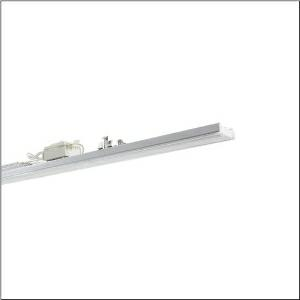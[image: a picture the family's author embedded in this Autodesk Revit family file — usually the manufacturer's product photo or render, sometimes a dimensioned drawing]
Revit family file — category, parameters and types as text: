
# Revit family: licross_r__21_recessed_mo_52te12dn4axg3c_0e6c
name_source: partatom
category: Lighting Fixtures
units: mm (PartAtom-declared; Revit-internal decimal feet)

## family parameters
Cut with Voids When Loaded = No
Host = Face
Light Source = No
Part Type = Normal
Room Calculation Point = No
Round Connector Dimension = Use Diameter
Shared = No

## types (1)
- --- (1 x LED, 950 lm, 6.7 W, 4000K)
    Apparent Load = 7 VA
    CIE Flux Codes = 72 92 99 100 100
    Color Rendering = 80
    Color Temperature = 4000K
    Default Elevation = 1800 mm
    Description = Licross® 21 Recessed MO, luminaire insert, of sheet steel, galvanised, coil coated, white, length: 1.500mm, width: 66mm, height: 67mm, LED rated luminous flux: 10.280lm, light colour: 840, control gear: DALI 2 (for two DALI lines), with plug, 6-pole, with phase selection, for trunking rail, 14-core, mains connection: 220..240V, AC, 50/60Hz, rated input power: 62W, internal wiring halogen-free, for emergency light function, for trunking rail, 14-core, converter,control gear: single battery element, battery: LiFePO4, 9Ah, primary optical cover: cover, of PMMA, light emission: direct distribution, primary light characteristic: symmetric, protection rating (complete): IP54, insulation class (complete): insulation class I (protective earthing), certification: CE, UKCA, protection symbol: D if used in an environment with non-conductive dust loads with corresponding accessories, impact resistance: IK06, permissible ambient temperature for indoor applications: +5..+35°C, standard: EN 60598-2-22, LABS conformity tested according to VDMA 24364:2018-05, reducing of maximum allowable ambient temperature of 5°C with ceiling mounting, corresponds to IFS (International Featured Standards) requirements for safety and quality in the food industry, packaging unit: 1 piece
    Height = 58 mm
    Lamp = 1 x LED
    Lamp Light Flux = 950 lm
    Lamp Power = 6.7 W
    Lamp count = 1
    Length = 1500 mm
    Luminous efficacy = 142 lm/W
    Manufacturer = Siteco
    ModVariant = No
    Model = 52TE12DN4AXG3C
    Mounting Place = Ceiling
    Mounting Type = Pendant
    Number of Poles = 1
    OnlyDefault = Yes
    Power Factor = 1
    Product Name = Licross® 21 Recessed MO
    Product group = luminaire insert | ceiling pendant
    ProductGroupID = 902
    Protection Class = Protection class I
    Protection Degree = IP 54
    RLX_Detail_Level = 1
    RLX_Emergency_Light_Flux = 0 lm
    RLX_Emergency_Type = 0
    RLX_Emergency_Type_DB = No
    RlxData = <blob elided: 25113 chars, md5=1fc3aedb>
    Socket = socket
    Standby Power = 0 W
    System Light Flux = 950 lm
    System Power = 7 W
    Type Comments = : emergency light operation: 3 h
    Type Image = l_1296930.jpg
    URL = http://relux.com
    VarID = @adj_131531
    Voltage = 0 V
    Weight = 0.00 kg
    Width = 66 mm

## geometry (parser evidence)
native form markers: Blend x4, Sweep x11
no freeform markers — native parametric forms only
